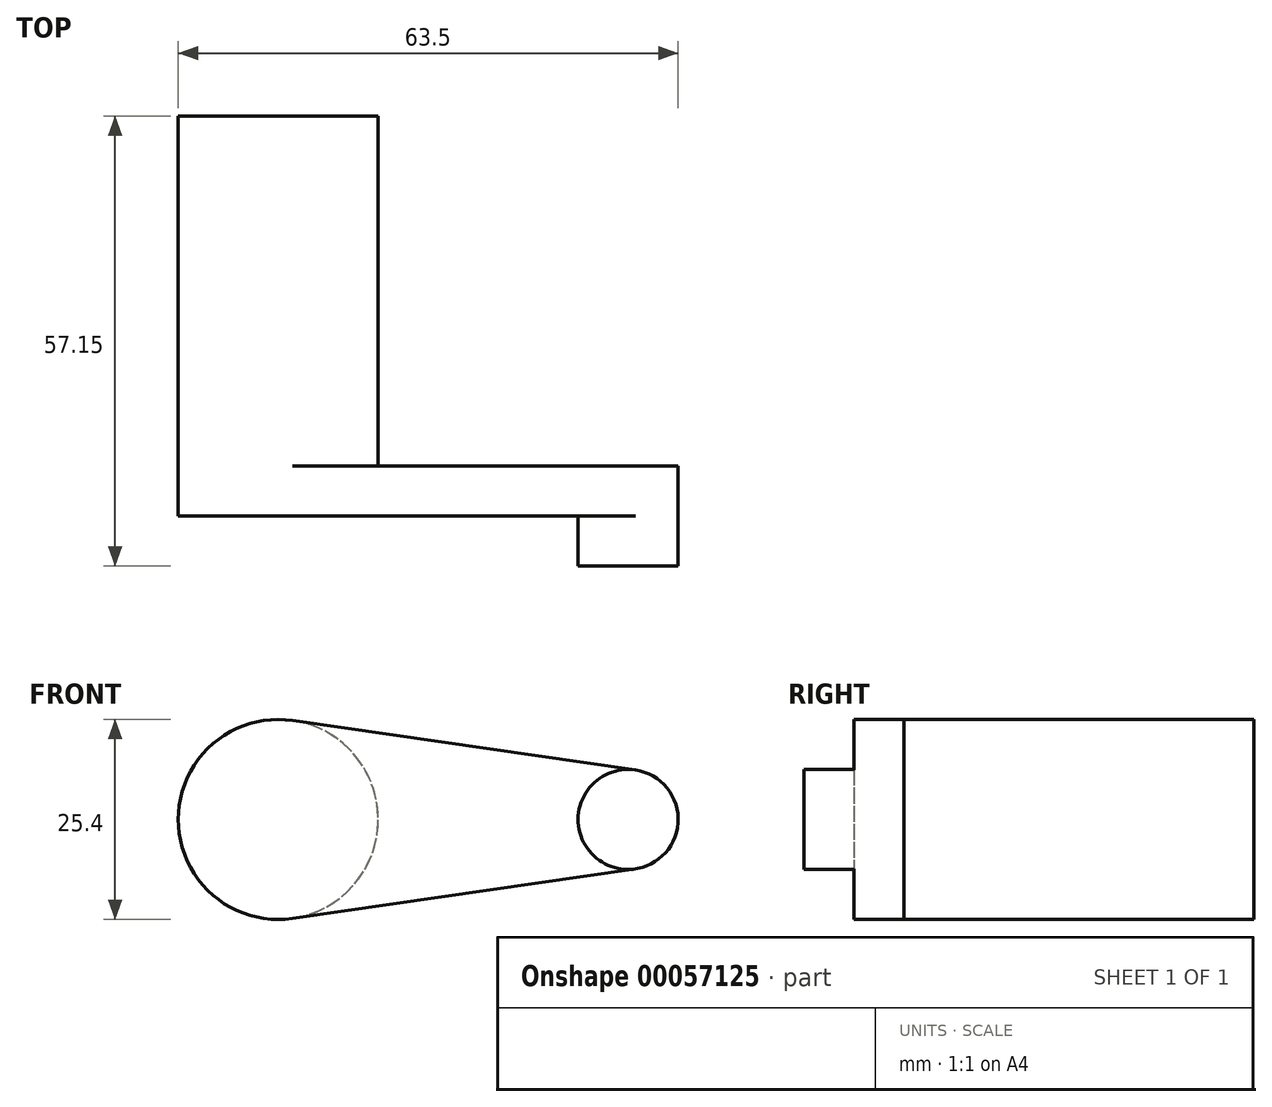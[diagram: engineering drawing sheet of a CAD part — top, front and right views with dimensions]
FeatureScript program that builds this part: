
annotation { "Feature Type Name" : "Feature", "Feature Type Description" : "" }
export const myFeature = defineFeature(function(context is Context, id is Id, definition is map)
    precondition{}
    {
        {
            var Q0;
            Q0=qCreatedBy(makeId("Front.planeOp"),FACE);
            var sketch = newSketch(context, id + "F0", { "sketchPlane" : qUnion([Q0])});
            skCircle(sketch, "E0", {"center": v(0, 0) * mm, "radius": 12.7 * mm});
            skCircle(sketch, "E1", {"center": v(44.45, 0) * mm, "radius": 6.35 * mm});
            skLineSegment(sketch, "E2", {"start": v(12.7, 0) * mm, "end": v(38.1, 0) * mm});
            skLineSegment(sketch, "E3", {"start": v(45.36, 6.28) * mm, "end": v(1.81, 12.57) * mm});
            skLineSegment(sketch, "E4", {"start": v(1.81, -12.57) * mm, "end": v(45.36, -6.28) * mm});
            skSolve(sketch);
        }
        {
            var Q0;
            Q0=makeQuery(id+"F0.imprint","IMPRINT",FACE,{"disambiguationData":[TD([[makeQuery(id+"F0.imprint","IMPRINT",EDGE,{"derivedFrom":sQuery(id+"F0.wireOp",EDGE,"E0")}),1.0]])]});
            extrude(context, id + "F1", {"entities" : qUnion([Q0]), "depth" : 50.8 * mm});
        }
        {
            var Q0;
            {var subQ0=sQuery(id+"F0.wireOp",EDGE,"E2");Q0=makeQuery(id+"F0.imprint","IMPRINT",FACE,{"disambiguationData":[TD([[makeQuery(id+"F0.imprint","IMPRINT",EDGE,{"derivedFrom":subQ0}),1.0]])]});}
            var Q1;
            {var subQ0=sQuery(id+"F0.wireOp",EDGE,"E2");Q1=makeQuery(id+"F0.imprint","IMPRINT",FACE,{"disambiguationData":[TD([[makeQuery(id+"F0.imprint","IMPRINT",EDGE,{"derivedFrom":subQ0}),-1.0]])]});}
            var Q2;
            {var subQ0=sQuery(id+"F0.wireOp",EDGE,"E1");var subQ1=makeQuery(id+"F0.imprint","INTERSECT",VERTEX,{"derivedFrom":[subQ0,sQuery(id+"F0.wireOp",EDGE,"E2")]});Q2=makeQuery(id+"F0.imprint","IMPRINT",FACE,{"disambiguationData":[TD([[makeQuery(id+"F0.imprint","IMPRINT",EDGE,{"disambiguationData":[TD([[subQ1,1.0]])],"derivedFrom":subQ0}),1.0]])]});}
            extrude(context, id + "F2", {"entities" : qUnion([Q0, Q1, Q2]), "operationType" : NewBodyOperationType.ADD, "depth" : 50.8 * mm, "hasSecondDirection" : true, "secondDirectionOppositeDirection" : false, "secondDirectionDepth" : 44.45 * mm});
        }
        {
            var Q0;
            {var subQ0=sQuery(id+"F0.wireOp",EDGE,"E1");var subQ1=makeQuery(id+"F0.imprint","INTERSECT",VERTEX,{"derivedFrom":[subQ0,sQuery(id+"F0.wireOp",EDGE,"E2")]});Q0=makeQuery(id+"F0.imprint","IMPRINT",FACE,{"disambiguationData":[TD([[makeQuery(id+"F0.imprint","IMPRINT",EDGE,{"disambiguationData":[TD([[subQ1,1.0]])],"derivedFrom":subQ0}),1.0]])]});}
            extrude(context, id + "F3", {"entities" : qUnion([Q0]), "operationType" : NewBodyOperationType.ADD, "depth" : 57.15 * mm, "hasSecondDirection" : true, "secondDirectionOppositeDirection" : false, "secondDirectionDepth" : 50.8 * mm});
        }
    });
